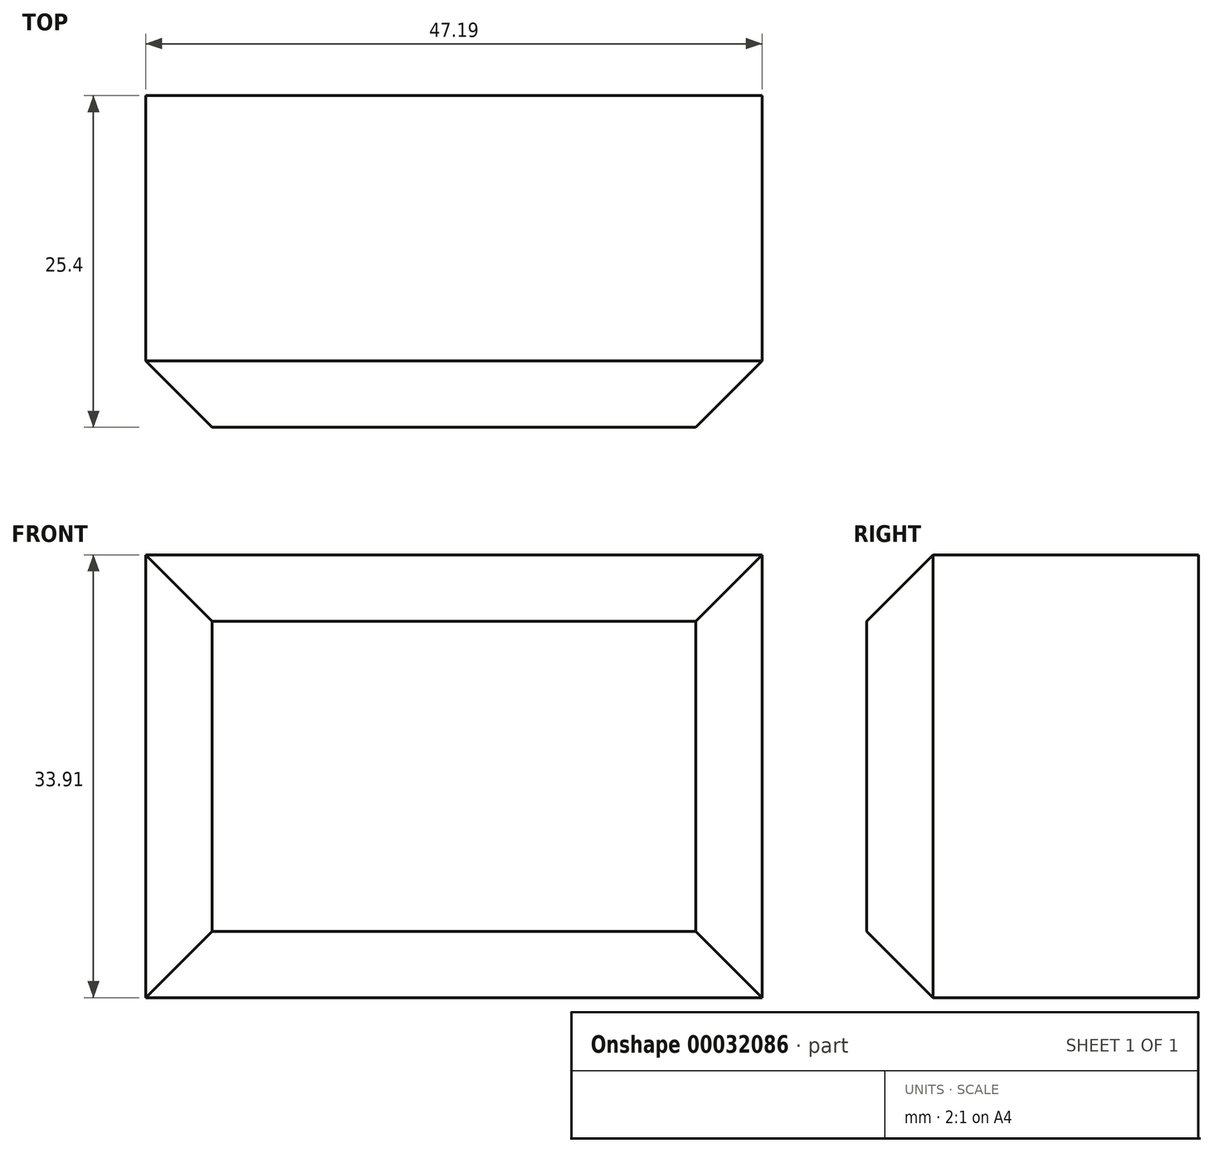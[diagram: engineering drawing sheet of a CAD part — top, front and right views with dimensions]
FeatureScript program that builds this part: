
annotation { "Feature Type Name" : "Feature", "Feature Type Description" : "" }
export const myFeature = defineFeature(function(context is Context, id is Id, definition is map)
    precondition{}
    {
        {
            var Q0;
            Q0=qCreatedBy(makeId("Front.planeOp"),FACE);
            var sketch = newSketch(context, id + "F0", { "sketchPlane" : qUnion([Q0])});
            skLineSegment(sketch, "E0.bottom", {"start": v(0, 0) * mm, "end": v(47.2, 0) * mm});
            skLineSegment(sketch, "E0.top", {"start": v(0, 33.91) * mm, "end": v(47.2, 33.91) * mm});
            skLineSegment(sketch, "E0.left", {"start": v(0, 0) * mm, "end": v(0, 33.91) * mm});
            skLineSegment(sketch, "E0.right", {"start": v(47.2, 0) * mm, "end": v(47.2, 33.91) * mm});
            skSolve(sketch);
        }
        {
            var Q0;
            Q0 = qSketchRegion(id + "F0", true);
            extrude(context, id + "F1", {"entities" : qUnion([Q0]), "depth" : 25.4 * mm});
        }
        {
            var Q0;
            Q0=makeQuery(id+"F1.opExtrude","CAP_FACE",FACE,{"disambiguationData":[OSD([sQuery(id+"F0.wireOp",EDGE,"E0.bottom"),sQuery(id+"F0.wireOp",EDGE,"E0.top"),sQuery(id+"F0.wireOp",EDGE,"E0.left"),sQuery(id+"F0.wireOp",EDGE,"E0.right")])],"isStart":false});
            var sketch = newSketch(context, id + "F2", { "sketchPlane" : qUnion([Q0])});
            skCircle(sketch, "E1", {"center": v(22.95, 19.22) * mm, "radius": 10.2 * mm});
            skSolve(sketch);
        }
        {
            var Q0;
            Q0=makeQuery(id+"F1.opExtrude","CAP_EDGE",EDGE,{"disambiguationData":[OSD([sQuery(id+"F0.wireOp",EDGE,"E0.top")])],"isStart":false});
            var Q1;
            Q1=makeQuery(id+"F1.opExtrude","CAP_EDGE",EDGE,{"disambiguationData":[OSD([sQuery(id+"F0.wireOp",EDGE,"E0.left")])],"isStart":false});
            var Q2;
            Q2=makeQuery(id+"F1.opExtrude","CAP_EDGE",EDGE,{"disambiguationData":[OSD([sQuery(id+"F0.wireOp",EDGE,"E0.bottom")])],"isStart":false});
            var Q3;
            Q3=makeQuery(id+"F1.opExtrude","CAP_EDGE",EDGE,{"disambiguationData":[OSD([sQuery(id+"F0.wireOp",EDGE,"E0.right")])],"isStart":false});
            chamfer(context, id + "F3", {"entities" : qUnion([Q0, Q1, Q2, Q3]), "width" : 5.08 * mm, "tangentPropagation" : true});
        }
    });
